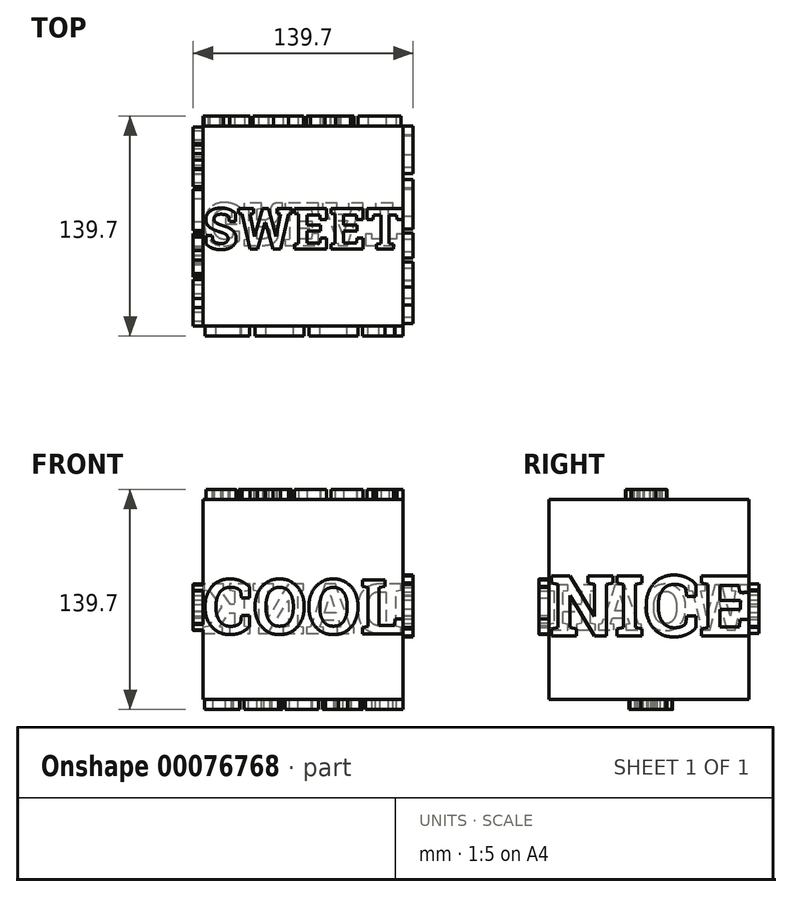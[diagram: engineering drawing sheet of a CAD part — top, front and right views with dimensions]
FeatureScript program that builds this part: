
annotation { "Feature Type Name" : "Feature", "Feature Type Description" : "" }
export const myFeature = defineFeature(function(context is Context, id is Id, definition is map)
    precondition{}
    {
        {
            var Q0;
            Q0=qCreatedBy(makeId("Front.planeOp"),FACE);
            var sketch = newSketch(context, id + "F0", { "sketchPlane" : qUnion([Q0])});
            skLineSegment(sketch, "E0.bottom", {"start": v(-62.2, 66.62) * mm, "end": v(64.8, 66.62) * mm});
            skLineSegment(sketch, "E0.top", {"start": v(-62.2, -60.38) * mm, "end": v(64.8, -60.38) * mm});
            skLineSegment(sketch, "E0.left", {"start": v(-62.2, 66.62) * mm, "end": v(-62.2, -60.38) * mm});
            skLineSegment(sketch, "E0.right", {"start": v(64.8, 66.62) * mm, "end": v(64.8, -60.38) * mm});
            skSolve(sketch);
        }
        {
            var Q0;
            Q0=makeQuery(id+"F0.imprint","IMPRINT",FACE,{"disambiguationData":[TD([[makeQuery(id+"F0.imprint","IMPRINT",EDGE,{"derivedFrom":sQuery(id+"F0.wireOp",EDGE,"E0.bottom")}),-1.0]])]});
            extrude(context, id + "F1", {"entities" : qUnion([Q0]), "depth" : 127 * mm});
        }
        {
            var Q0;
            Q0=makeQuery(id+"F1.opExtrude","CAP_FACE",FACE,{"disambiguationData":[OSD([sQuery(id+"F0.wireOp",EDGE,"E0.bottom"),sQuery(id+"F0.wireOp",EDGE,"E0.top"),sQuery(id+"F0.wireOp",EDGE,"E0.left"),sQuery(id+"F0.wireOp",EDGE,"E0.right")])],"isStart":false});
            var sketch = newSketch(context, id + "F2", { "sketchPlane" : qUnion([Q0])});
            skText(sketch, "E1", { "text": "COOL", "fontName": "RobotoSlab-Bold.ttf"});
            const initialGuessF2  = {"E1": [-0.0622, -0.01873, 1, 0, 0.03485]};
            skSetInitialGuess(sketch, initialGuessF2);
            skSolve(sketch);
        }
        {
            var Q0;
            Q0 = qSketchRegion(id + "F2", true);
            extrude(context, id + "F3", {"entities" : qUnion([Q0]), "operationType" : NewBodyOperationType.ADD, "depth" : 6.35 * mm});
        }
        {
            var Q0;
            Q0=makeQuery(id+"F3.boolean.opBoolean","MERGE",FACE,{"derivedFrom":[makeQuery(id+"F1.opExtrude","SWEPT_FACE",FACE,{"disambiguationData":[OSD([sQuery(id+"F0.wireOp",EDGE,"E0.right")])]}),makeQuery(id+"F3.opExtrude","SWEPT_FACE",FACE,{"disambiguationData":[OSD([sQuery(id+"F2.wireOp",EDGE,"E1.sketch_text.stroke-78")])]})]});
            var sketch = newSketch(context, id + "F4", { "sketchPlane" : qUnion([Q0])});
            skText(sketch, "E2", { "text": "NICE", "fontName": "RobotoSlab-Bold.ttf"});
            const initialGuessF4  = {"E2": [-0.127, -0.02018, 1, 0, 0.03877]};
            skSetInitialGuess(sketch, initialGuessF4);
            skSolve(sketch);
        }
        {
            var Q0;
            Q0 = qSketchRegion(id + "F4", true);
            extrude(context, id + "F5", {"entities" : qUnion([Q0]), "operationType" : NewBodyOperationType.ADD, "depth" : 6.35 * mm});
        }
        {
            var Q0;
            Q0=makeQuery(id+"F5.boolean.opBoolean","MERGE",FACE,{"derivedFrom":[makeQuery(id+"F1.opExtrude","CAP_FACE",FACE,{"disambiguationData":[OSD([sQuery(id+"F0.wireOp",EDGE,"E0.bottom"),sQuery(id+"F0.wireOp",EDGE,"E0.top"),sQuery(id+"F0.wireOp",EDGE,"E0.left"),sQuery(id+"F0.wireOp",EDGE,"E0.right")])],"isStart":true}),makeQuery(id+"F5.opExtrude","SWEPT_FACE",FACE,{"disambiguationData":[OSD([sQuery(id+"F4.wireOp",EDGE,"E2.sketch_text.stroke-65")])]})]});
            var sketch = newSketch(context, id + "F6", { "sketchPlane" : qUnion([Q0])});
            skText(sketch, "E3", { "text": "DANK", "fontName": "RobotoSlab-Bold.ttf"});
            const initialGuessF6  = {"E3": [-0.0648, -0.01846, 1, 0, 0.03176]};
            skSetInitialGuess(sketch, initialGuessF6);
            skSolve(sketch);
        }
        {
            var Q0;
            Q0 = qSketchRegion(id + "F6", true);
            extrude(context, id + "F7", {"entities" : qUnion([Q0]), "operationType" : NewBodyOperationType.ADD, "depth" : 6.35 * mm});
        }
        {
            var Q0;
            Q0=makeQuery(id+"F1.opExtrude","SWEPT_FACE",FACE,{"disambiguationData":[OSD([sQuery(id+"F0.wireOp",EDGE,"E0.top")])]});
            var sketch = newSketch(context, id + "F8", { "sketchPlane" : qUnion([Q0])});
            skText(sketch, "E4", { "text": "GREAT", "fontName": "RobotoSlab-Bold.ttf"});
            const initialGuessF8  = {"E4": [-0.0622, 0.0489, 1, 0, 0.02723]};
            skSetInitialGuess(sketch, initialGuessF8);
            skSolve(sketch);
        }
        {
            var Q0;
            Q0 = qSketchRegion(id + "F8", true);
            extrude(context, id + "F9", {"entities" : qUnion([Q0]), "operationType" : NewBodyOperationType.ADD, "depth" : 6.35 * mm});
        }
        {
            var Q0;
            Q0=makeQuery(id+"F1.opExtrude","SWEPT_FACE",FACE,{"disambiguationData":[OSD([sQuery(id+"F0.wireOp",EDGE,"E0.bottom")])]});
            var sketch = newSketch(context, id + "F10", { "sketchPlane" : qUnion([Q0])});
            skText(sketch, "E5", { "text": "SWEET", "fontName": "RobotoSlab-Bold.ttf"});
            const initialGuessF10  = {"E5": [-0.0622, -0.07817, 1, 0, 0.02612]};
            skSetInitialGuess(sketch, initialGuessF10);
            skSolve(sketch);
        }
        {
            var Q0;
            Q0 = qSketchRegion(id + "F10", true);
            extrude(context, id + "F11", {"entities" : qUnion([Q0]), "operationType" : NewBodyOperationType.ADD, "depth" : 6.35 * mm});
        }
        {
            var Q0;
            Q0=makeQuery(id+"F7.boolean.opBoolean","MERGE",FACE,{"derivedFrom":[makeQuery(id+"F1.opExtrude","SWEPT_FACE",FACE,{"disambiguationData":[OSD([sQuery(id+"F0.wireOp",EDGE,"E0.left")])]}),makeQuery(id+"F7.opExtrude","SWEPT_FACE",FACE,{"disambiguationData":[OSD([sQuery(id+"F6.wireOp",EDGE,"E3.sketch_text.stroke-83")])]})]});
            var sketch = newSketch(context, id + "F12", { "sketchPlane" : qUnion([Q0])});
            skText(sketch, "E6", { "text": "WOAH", "fontName": "RobotoSlab-Bold.ttf"});
            const initialGuessF12  = {"E6": [0, -0.01628, 1, 0, 0.0291]};
            skSetInitialGuess(sketch, initialGuessF12);
            skSolve(sketch);
        }
        {
            var Q0;
            Q0 = qSketchRegion(id + "F12", true);
            extrude(context, id + "F13", {"entities" : qUnion([Q0]), "operationType" : NewBodyOperationType.ADD, "depth" : 6.35 * mm});
        }
    });
